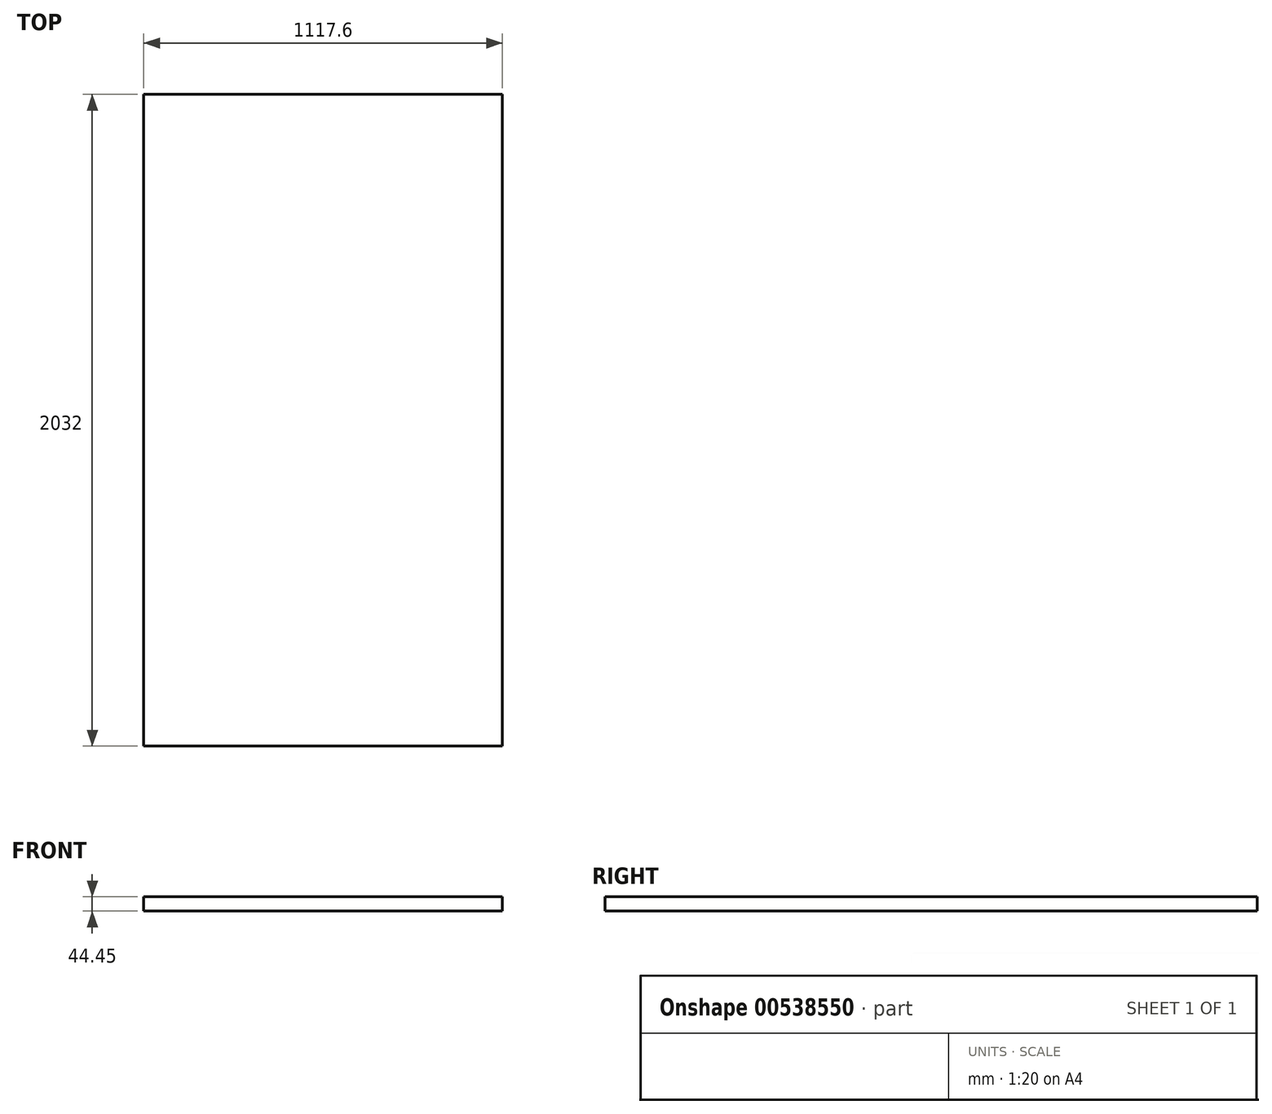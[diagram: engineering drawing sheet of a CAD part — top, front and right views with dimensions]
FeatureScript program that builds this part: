
annotation { "Feature Type Name" : "Feature", "Feature Type Description" : "" }
export const myFeature = defineFeature(function(context is Context, id is Id, definition is map)
    precondition{}
    {
        {
            var Q0;
            Q0=qCreatedBy(makeId("Top.planeOp"),FACE);
            var sketch = newSketch(context, id + "F0", { "sketchPlane" : qUnion([Q0])});
            skLineSegment(sketch, "E0.bottom", {"start": v(-558.8, 1016) * mm, "end": v(558.8, 1016) * mm});
            skLineSegment(sketch, "E0.top", {"start": v(-558.8, -1016) * mm, "end": v(558.8, -1016) * mm});
            skLineSegment(sketch, "E0.left", {"start": v(-558.8, 1016) * mm, "end": v(-558.8, -1016) * mm});
            skLineSegment(sketch, "E0.right", {"start": v(558.8, 1016) * mm, "end": v(558.8, -1016) * mm});
            skPoint(sketch, "E0.middle", {"position": v(0, 0) * mm});
            skSolve(sketch);
        }
        {
            var Q0;
            Q0=makeQuery(id+"F0.imprint","IMPRINT",FACE,{"disambiguationData":[TD([[makeQuery(id+"F0.imprint","IMPRINT",EDGE,{"derivedFrom":sQuery(id+"F0.wireOp",EDGE,"E0.bottom")}),-1.0]])]});
            extrude(context, id + "F1", {"entities" : qUnion([Q0]), "depth" : 44.45 * mm, "offsetDistance" : 25.4 * mm});
        }
    });
